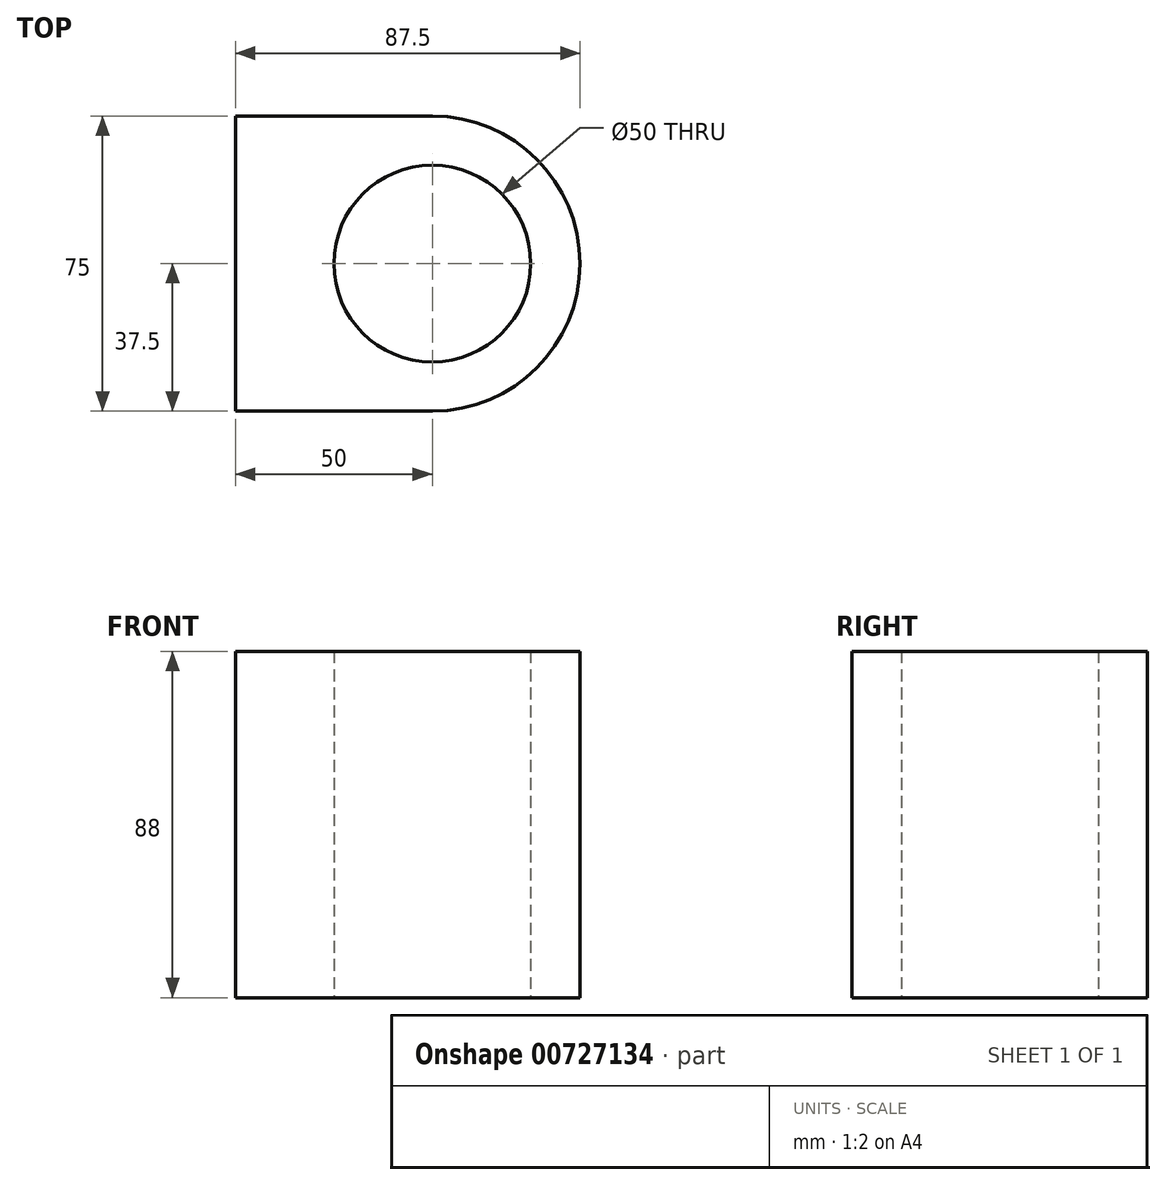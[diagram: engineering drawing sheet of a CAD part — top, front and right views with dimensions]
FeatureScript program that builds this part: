
annotation { "Feature Type Name" : "Feature", "Feature Type Description" : "" }
export const myFeature = defineFeature(function(context is Context, id is Id, definition is map)
    precondition{}
    {
        {
            var Q0;
            Q0=qCreatedBy(makeId("Top.planeOp"),FACE);
            var sketch = newSketch(context, id + "F0", { "sketchPlane" : qUnion([Q0])});
            skLineSegment(sketch, "E0.bottom", {"start": v(0, 0) * mm, "end": v(50, 0) * mm});
            skLineSegment(sketch, "E0.top", {"start": v(0, 75) * mm, "end": v(50, 75) * mm});
            skLineSegment(sketch, "E0.left", {"start": v(0, 0) * mm, "end": v(0, 75) * mm});
            skLineSegment(sketch, "E0.right", {"start": v(50, 12.5) * mm, "end": v(50, 62.5) * mm});
            skCircle(sketch, "E1", {"center": v(50, 37.5) * mm, "radius": 25 * mm});
            skArc(sketch, "E2", {"start": v(50, 0) * mm, "mid": v(87.5, 37.5) * mm, "end": v(50, 75) * mm});
            skSolve(sketch);
        }
        {
            var Q0;
            Q0 = qSketchRegion(id + "F0", true);
            extrude(context, id + "F1", {"entities" : qUnion([Q0]), "depth" : 88 * mm, "offsetDistance" : 25 * mm});
        }
    });
